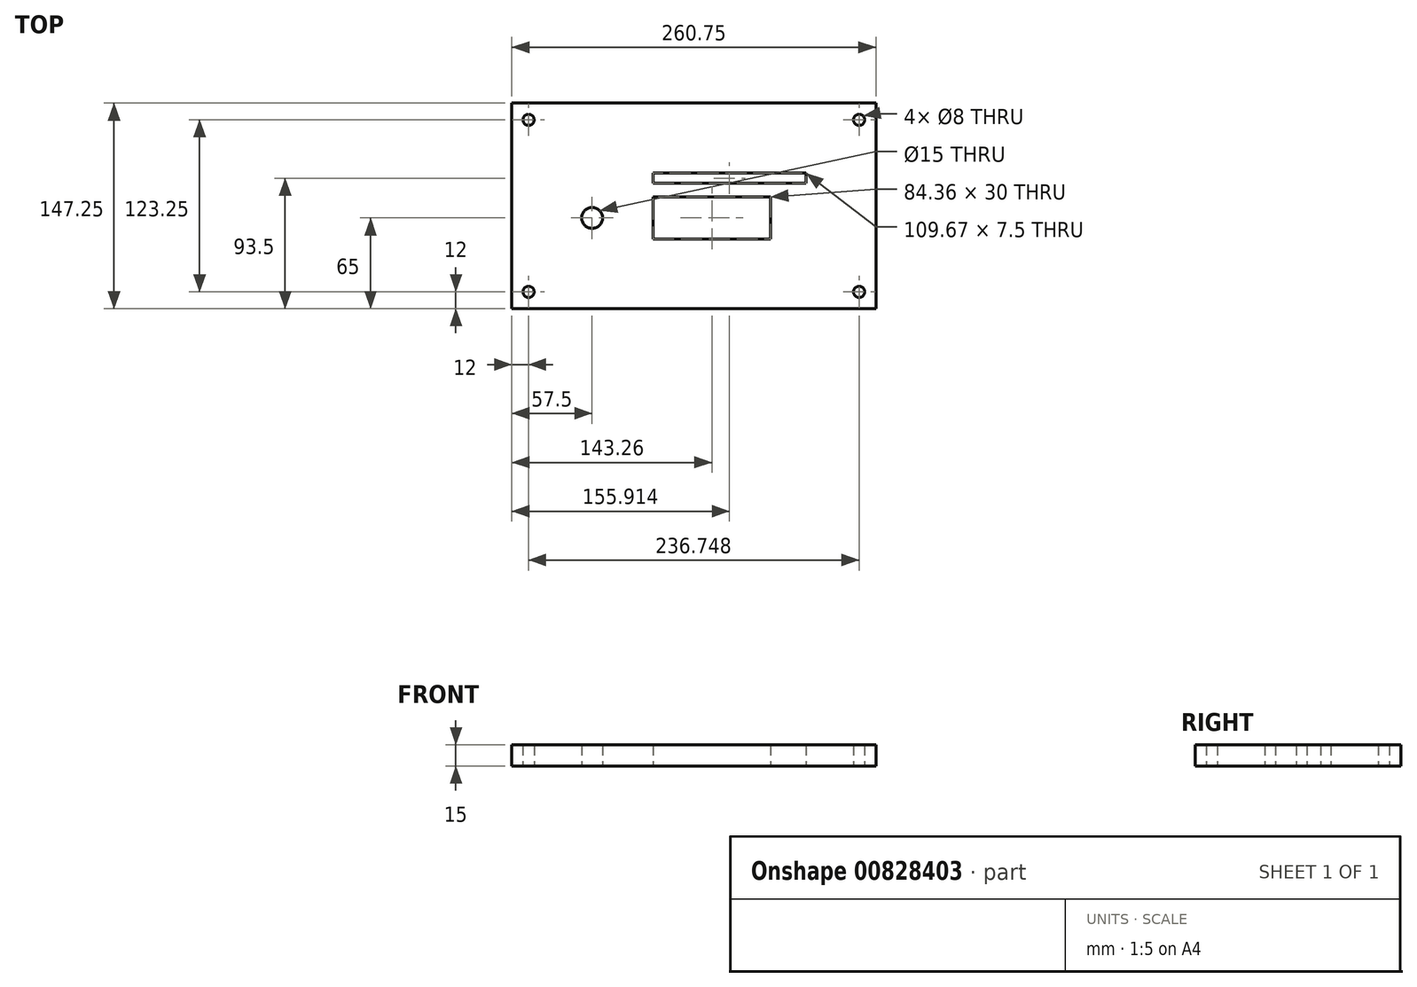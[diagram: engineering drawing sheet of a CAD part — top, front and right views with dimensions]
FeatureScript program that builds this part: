
annotation { "Feature Type Name" : "Feature", "Feature Type Description" : "" }
export const myFeature = defineFeature(function(context is Context, id is Id, definition is map)
    precondition{}
    {
        {
            var Q0;
            Q0=qCreatedBy(makeId("Top.planeOp"),FACE);
            var sketch = newSketch(context, id + "F0", { "sketchPlane" : qUnion([Q0])});
            skLineSegment(sketch, "E0.bottom", {"start": v(0, 0) * mm, "end": v(260.75, 0) * mm});
            skLineSegment(sketch, "E0.top", {"start": v(0, 147.25) * mm, "end": v(260.75, 147.25) * mm});
            skLineSegment(sketch, "E0.left", {"start": v(0, 0) * mm, "end": v(0, 147.25) * mm});
            skLineSegment(sketch, "E0.right", {"start": v(260.75, 0) * mm, "end": v(260.75, 147.25) * mm});
            skCircle(sketch, "E1", {"center": v(57.5, 65) * mm, "radius": 7.5 * mm});
            skLineSegment(sketch, "E2.bottom", {"start": v(101.08, 80) * mm, "end": v(185.44, 80) * mm});
            skLineSegment(sketch, "E2.top", {"start": v(101.08, 50) * mm, "end": v(185.44, 50) * mm});
            skLineSegment(sketch, "E2.left", {"start": v(101.08, 80) * mm, "end": v(101.08, 50) * mm});
            skLineSegment(sketch, "E2.right", {"start": v(185.44, 80) * mm, "end": v(185.44, 50) * mm});
            skLineSegment(sketch, "E3.bottom", {"start": v(101.08, 97.25) * mm, "end": v(210.75, 97.25) * mm});
            skLineSegment(sketch, "E3.top", {"start": v(101.08, 89.75) * mm, "end": v(210.75, 89.75) * mm});
            skLineSegment(sketch, "E3.left", {"start": v(101.08, 97.25) * mm, "end": v(101.08, 89.75) * mm});
            skLineSegment(sketch, "E3.right", {"start": v(210.75, 97.25) * mm, "end": v(210.75, 89.75) * mm});
            skCircle(sketch, "E4", {"center": v(12, 135.25) * mm, "radius": 4 * mm});
            skCircle(sketch, "E5", {"center": v(248.75, 135.25) * mm, "radius": 4 * mm});
            skCircle(sketch, "E6", {"center": v(248.75, 12) * mm, "radius": 4 * mm});
            skCircle(sketch, "E7", {"center": v(12, 12) * mm, "radius": 4 * mm});
            skSolve(sketch);
        }
        {
            var Q0;
            Q0=makeQuery(id+"F0.imprint","IMPRINT",FACE,{"disambiguationData":[TD([[makeQuery(id+"F0.imprint","IMPRINT",EDGE,{"derivedFrom":sQuery(id+"F0.wireOp",EDGE,"E0.bottom")}),1.0]])]});
            extrude(context, id + "F1", {"entities" : qUnion([Q0]), "depth" : 15 * mm, "offsetDistance" : 25 * mm});
        }
    });
